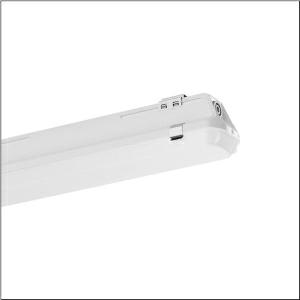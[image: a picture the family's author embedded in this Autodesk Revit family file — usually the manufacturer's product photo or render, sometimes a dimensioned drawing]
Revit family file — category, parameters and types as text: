
# Revit family: monsun_r__21_51fb107l420j_9cfc
name_source: partatom
category: Lighting Fixtures
units: mm (PartAtom-declared; Revit-internal decimal feet)

## family parameters
Cut with Voids When Loaded = No
Host = Face
Light Source = No
Part Type = Normal
Room Calculation Point = No
Round Connector Dimension = Use Diameter
Shared = No

## types (1)
- Monsun® 21 (1 x LED, 2590 lm, 17.7 W, 4000K)
    Apparent Load = 18 VA
    CIE Flux Codes = 46 76 93 94 100
    Color Rendering = 80
    Color Temperature = 4000K
    Default Elevation = 1800 mm
    Description = Monsun® 21, damp-proof luminaire, chain hanger, primary optical cover: enclosure, of PMMA, light emission: direct distribution, primary light characteristic: symmetric, installation type: suspended mounting, surface-mounted, horizontal mounting, vertical mounting, LED, rated luminous flux: 2.590lm, luminous efficacy: 144lm/W, light colour: 840, colour temperature: 4000K, control gear: ECG, with terminal, 3-pole, max. 2.5mm², mains connection: 220..240V, AC, 50/60Hz, rated input power: 18W, housing, of glass-fibre reinforced plastic, uncoated, bright grey, incl. chain hanger, length: 1.299mm, width: 90mm, height: 88mm, clip for enclosure, of stainless steel (V2A), ceiling mounting element, of stainless steel (V2A), chain hanger, of stainless steel (V2A), protection rating (complete): IP66, insulation class (complete): insulation class I (protective earthing), certification: CE, ENEC, VDE, UKCA, protection symbol: D, impact resistance: IK04, permissible operating ambient temperature: -25..+35°C, standard: EN 50419, EN 60598-2-1, corresponds to IFS (International Featured Standards) requirements for safety and quality in the food industry, for indoor or canopied outdoor use, no direct snow, no direct sun, no direct rain, contact your sales advisor before using the luminaires in applications with unclear chemical exposure, large temperature fluctuations or condensation-forming humidity, LABS conformity tested according to VDMA 24364:2018-05, packaging unit: 1 piece
    Height = 88 mm
    Lamp = 1 x LED
    Lamp Light Flux = 2590 lm
    Lamp Power = 17.7 W
    Lamp count = 1
    Length = 1299 mm
    Luminous efficacy = 146 lm/W
    Manufacturer = Siteco
    ModVariant = No
    Model = 51FB107L420J
    Mounting Place = Ceiling
    Mounting Type = Surface mounted
    Number of Poles = 1
    OnlyDefault = Yes
    Power Factor = 1
    Product Name = Monsun® 21
    Product group = damp-proof luminaire
    ProductGroupID = 300
    Protection Class = Protection class I
    Protection Degree = IP 66
    RLX_Detail_Level = 1
    RLX_Emergency_Light_Flux = 0 lm
    RLX_Emergency_Type = 0
    RLX_Emergency_Type_DB = No
    RlxData = <blob elided: 89821 chars, md5=55bb28e9>
    Socket = socket
    Standby Power = 0 W
    System Light Flux = 2590 lm
    System Power = 18 W
    Type Comments = Product without accessories
    Type Image = l_1006717.jpg
    URL = http://relux.com
    VarID = ---
    Voltage = 0 V
    Weight = 0.00 kg
    Width = 90 mm

## geometry (parser evidence)
native form markers: Blend x4, Sweep x14
no freeform markers — native parametric forms only
